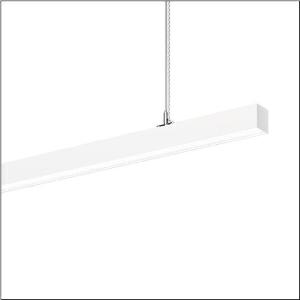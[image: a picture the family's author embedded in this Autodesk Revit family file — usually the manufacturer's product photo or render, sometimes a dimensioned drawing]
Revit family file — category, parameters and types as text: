
# Revit family: silica_r__21_51mx33tat7w_2751
name_source: partatom
category: Lighting Fixtures
units: mm (PartAtom-declared; Revit-internal decimal feet)

## family parameters
Cut with Voids When Loaded = No
Host = Face
Light Source = No
Part Type = Normal
Room Calculation Point = No
Round Connector Dimension = Use Diameter
Shared = No

## types (1)
- --- (1 x LED, 5740 lm, 53.8 W, 6500K)
    Apparent Load = 54 VA
    CIE Flux Codes = 78 96 99 56 100
    Color Rendering = 80
    Color Temperature = 6500K
    Default Elevation = 1800 mm
    Description = Silica® 21, office luminaire, primary optical cover: prismatic diffuser, of PMMA, CAT 2 (L<= 3000cd/m²), light emission: direct/indirect distribution, primary light characteristic: symmetric, installation type: suspended mounting, LED, rated luminous flux: 5.740lm, luminous efficacy: 102lm/W, light colour: 8tw, colour temperature: 2700..6500K, control gear: ECG DALI, with terminal, 3+2-pole, max. 2.5mm², mains connection: 220..240V, AC, 50/60Hz, rated input power: 56.5W, luminaire housing, of aluminium, traffic white (RAL 9016), length: 1.204mm, width: 53mm, height: 53mm, protection rating (complete): IP20, insulation class (complete): insulation class I (protective earthing), certification: CE, permissible operating ambient temperature: 0..+35°C, standard: EN 50419, packaging unit: 1 piece
    Height = 53 mm
    Lamp = 1 x LED
    Lamp Light Flux = 5740 lm
    Lamp Power = 53.8 W
    Lamp count = 1
    Length = 1204 mm
    Luminous efficacy = 107 lm/W
    Manufacturer = Siteco
    ModVariant = No
    Model = 51MX33TAT7W
    Mounting Place = Ceiling
    Mounting Type = Pendant
    Number of Poles = 1
    OnlyDefault = Yes
    Power Factor = 1
    Product Name = Silica® 21
    Product group = office luminaire | ceiling pendant
    ProductGroupID = 902
    Protection Class = Protection class I
    Protection Degree = IP 20
    RLX_Detail_Level = 1
    RLX_Emergency_Light_Flux = 0 lm
    RLX_Emergency_Type = 0
    RLX_Emergency_Type_DB = No
    RlxData = <blob elided: 18205 chars, md5=e0979a79>
    Socket = socket
    Standby Power = 0 W
    System Light Flux = 5740 lm
    System Power = 54 W
    Type Comments = individual setting
    Type Image = l_1313629.jpg
    URL = http://relux.com
    VarID = @adj_089151
    Voltage = 0 V
    Weight = 0.00 kg
    Width = 53 mm

## geometry (parser evidence)
native form markers: Blend x4, Sweep x13
no freeform markers — native parametric forms only
